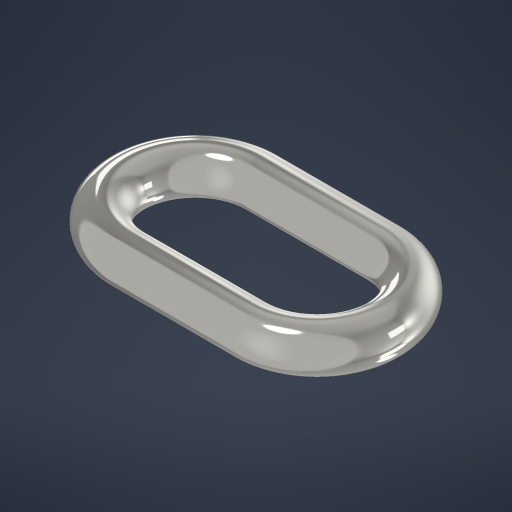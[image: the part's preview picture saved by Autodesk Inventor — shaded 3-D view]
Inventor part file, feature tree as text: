
AUTODESK INVENTOR PART (.ipt)
format: ipt  version: 2024 (Build 280153000, 153)  size: 312,320 bytes
history: native  units: mm
features: other x5, sweep x1, plane x1, sketch x1
ambient origin geometry x8: Origin, YZ Plane, XZ Plane, XY Plane, X Axis, Y Axis, Z Axis, Center Point
bodies: Body1 (feature_tree)
feature tree (8):
  other  "Sólido1"
  sweep  "Barrido1"
  plane  "Plano de trabajo1"
  sketch  "Boceto3"  dims[d0=16.0mm d1=4.0mm d2=19.0mm d3=2.0mm d4=4.0mm d5=0.0mm d6=0.0mm]
  other  "Punto de trabajo2"
  other  "Punto de trabajo3"
  other  "Punto de trabajo4"
  other  "Punto de trabajo5"
